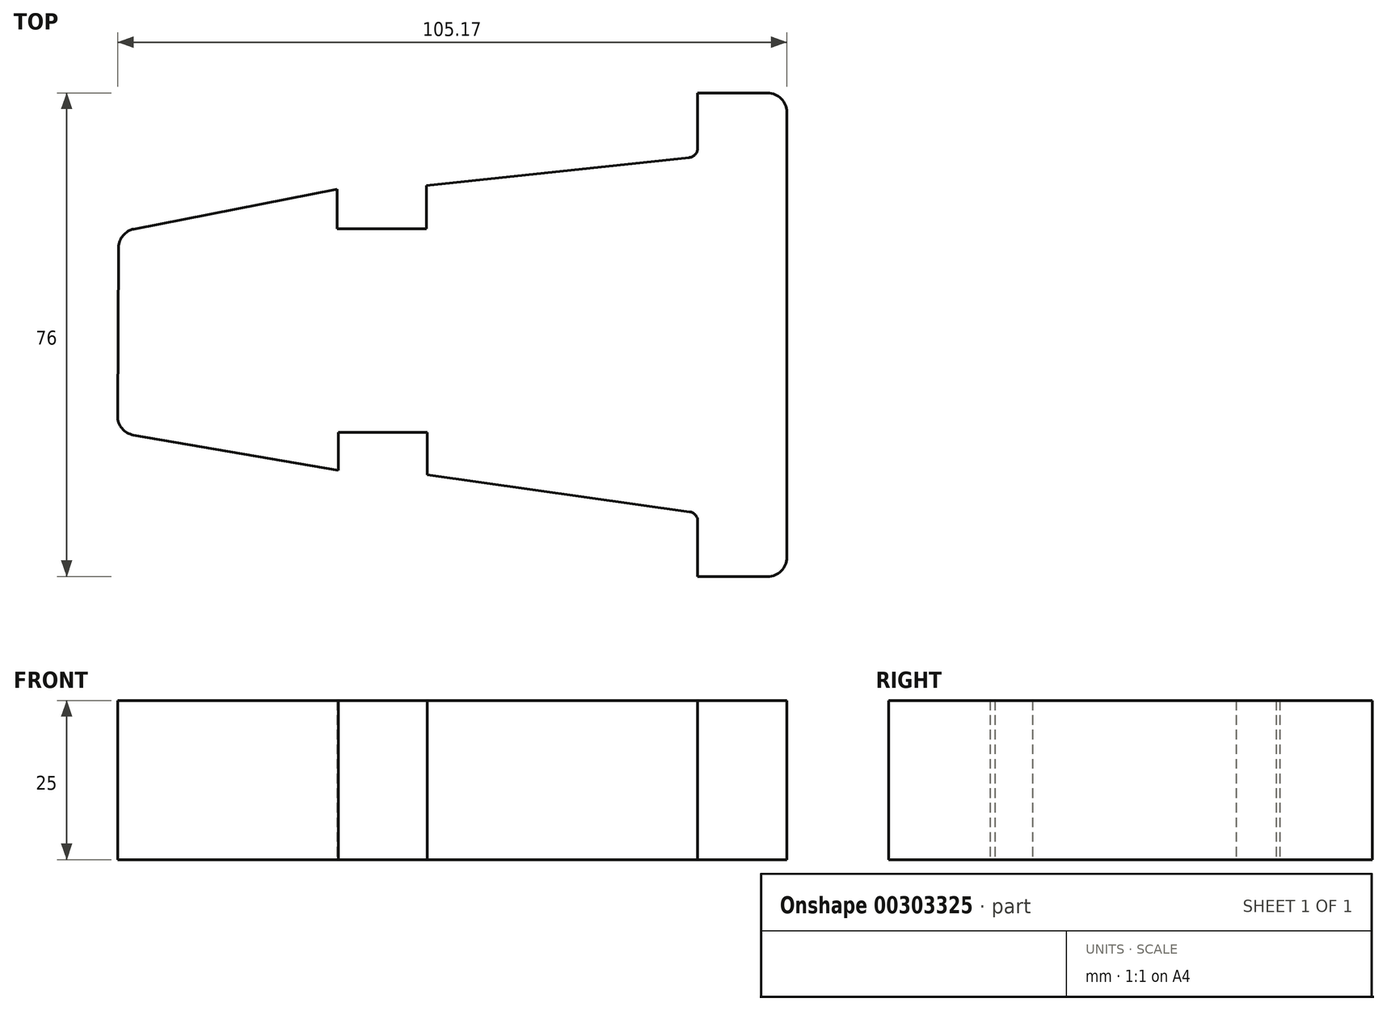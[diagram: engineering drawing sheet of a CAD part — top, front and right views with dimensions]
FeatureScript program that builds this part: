
annotation { "Feature Type Name" : "Feature", "Feature Type Description" : "" }
export const myFeature = defineFeature(function(context is Context, id is Id, definition is map)
    precondition{}
    {
        {
            var Q0;
            Q0=qCreatedBy(makeId("Top.planeOp"),FACE);
            var sketch = newSketch(context, id + "F0", { "sketchPlane" : qUnion([Q0])});
            skLineSegment(sketch, "E0", {"start": v(20.51, 43.2) * mm, "end": v(20.51, -26.8) * mm});
            skLineSegment(sketch, "E1", {"start": v(6.51, -29.8) * mm, "end": v(17.51, -29.8) * mm});
            skLineSegment(sketch, "E2", {"start": v(17.51, 46.2) * mm, "end": v(6.51, 46.2) * mm});
            skLineSegment(sketch, "E3", {"start": v(6.51, 46.2) * mm, "end": v(6.51, 37.56) * mm});
            skLineSegment(sketch, "E4", {"start": v(6.51, -29.8) * mm, "end": v(6.51, -21.1) * mm});
            skLineSegment(sketch, "E5", {"start": v(-36, -7.16) * mm, "end": v(-50, -7.16) * mm});
            skLineSegment(sketch, "E6", {"start": v(-50.14, 24.84) * mm, "end": v(-36.14, 24.84) * mm});
            skPoint(sketch, "E7.end.orphan", {"position": v(-50, -10.15) * mm});
            skLineSegment(sketch, "E8", {"start": v(-36.14, 24.84) * mm, "end": v(-36.14, 31.66) * mm});
            skLineSegment(sketch, "E9", {"start": v(-36.14, 31.66) * mm, "end": v(5.17, 36.07) * mm});
            skLineSegment(sketch, "E10", {"start": v(-36, -7.16) * mm, "end": v(-36, -13.82) * mm});
            skLineSegment(sketch, "E11", {"start": v(5.22, -19.61) * mm, "end": v(-36, -13.82) * mm});
            skLineSegment(sketch, "E12", {"start": v(-50.14, 24.84) * mm, "end": v(-50.14, 31.1) * mm});
            skLineSegment(sketch, "E13", {"start": v(-50, -7.16) * mm, "end": v(-50, -13.1) * mm});
            skLineSegment(sketch, "E14", {"start": v(-50, -13.1) * mm, "end": v(-82.17, -7.56) * mm});
            skLineSegment(sketch, "E15", {"start": v(-50.14, 31.1) * mm, "end": v(-82.08, 24.84) * mm});
            skLineSegment(sketch, "E16", {"start": v(-84.66, -4.58) * mm, "end": v(-84.5, 21.91) * mm});
            skPoint(sketch, "E17.visualSharp", {"position": v(20.51, 46.2) * mm});
            skArc(sketch, "E17.filletArc", {"start": v(20.51, 43.2) * mm, "mid": v(19.63, 45.33) * mm, "end": v(17.51, 46.2) * mm});
            skPoint(sketch, "E18.visualSharp", {"position": v(20.51, -29.8) * mm});
            skArc(sketch, "E18.filletArc", {"start": v(17.51, -29.8) * mm, "mid": v(19.63, -28.91) * mm, "end": v(20.51, -26.8) * mm});
            skPoint(sketch, "E19.visualSharp", {"position": v(-84.49, 24.37) * mm});
            skArc(sketch, "E19.filletArc", {"start": v(-82.08, 24.84) * mm, "mid": v(-83.81, 23.8) * mm, "end": v(-84.5, 21.91) * mm});
            skPoint(sketch, "E20.newPointB", {"position": v(-84.49, -7.16) * mm});
            skArc(sketch, "E20.filletArc", {"start": v(-84.66, -4.58) * mm, "mid": v(-83.96, -6.53) * mm, "end": v(-82.17, -7.56) * mm});
            skPoint(sketch, "E21.visualSharp", {"position": v(6.51, 36.2) * mm});
            skArc(sketch, "E21.filletArc", {"start": v(5.17, 36.07) * mm, "mid": v(6.13, 36.55) * mm, "end": v(6.51, 37.56) * mm});
            skPoint(sketch, "E22.visualSharp", {"position": v(6.51, -19.8) * mm});
            skArc(sketch, "E22.filletArc", {"start": v(6.51, -21.1) * mm, "mid": v(6.14, -20.11) * mm, "end": v(5.22, -19.61) * mm});
            skSolve(sketch);
        }
        {
            var Q0;
            Q0 = qSketchRegion(id + "F0", true);
            extrude(context, id + "F1", {"entities" : qUnion([Q0]), "depth" : 25 * mm});
        }
        {
            var Q0;
            Q0 = qSketchRegion(id + "F0", true);
            extrude(context, id + "F2", {"entities" : qUnion([Q0]), "operationType" : NewBodyOperationType.ADD, "depth" : 25 * mm});
        }
    });
